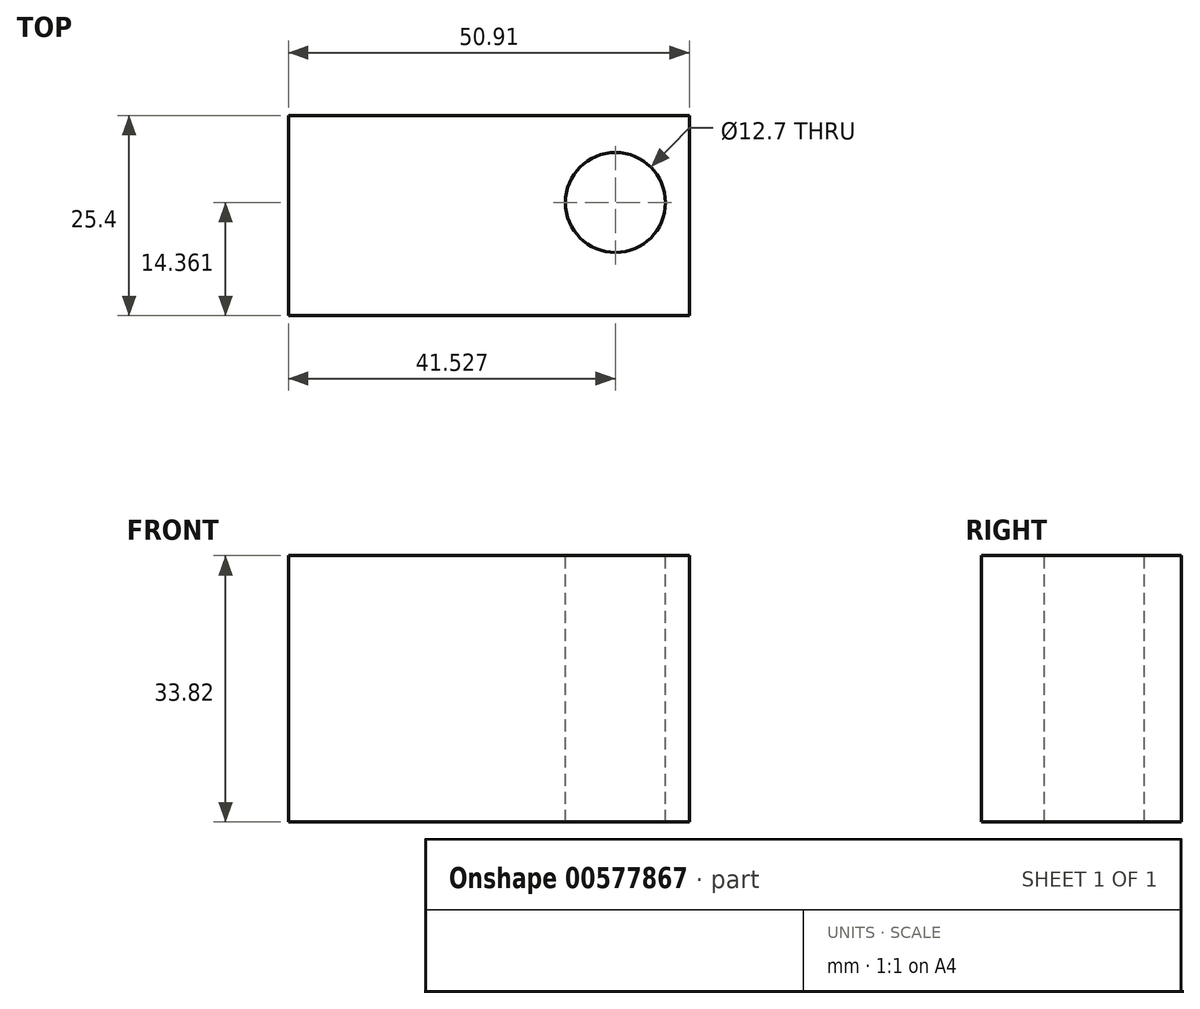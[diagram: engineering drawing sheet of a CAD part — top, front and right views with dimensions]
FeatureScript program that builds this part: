
annotation { "Feature Type Name" : "Feature", "Feature Type Description" : "" }
export const myFeature = defineFeature(function(context is Context, id is Id, definition is map)
    precondition{}
    {
        {
            var Q0;
            Q0=qCreatedBy(makeId("Front.planeOp"),FACE);
            var sketch = newSketch(context, id + "F0", { "sketchPlane" : qUnion([Q0])});
            skLineSegment(sketch, "E0.bottom", {"start": v(-50.91, 33.82) * mm, "end": v(0, 33.82) * mm});
            skLineSegment(sketch, "E0.top", {"start": v(-50.91, 0) * mm, "end": v(0, 0) * mm});
            skLineSegment(sketch, "E0.left", {"start": v(-50.91, 33.82) * mm, "end": v(-50.91, 0) * mm});
            skLineSegment(sketch, "E0.right", {"start": v(0, 33.82) * mm, "end": v(0, 0) * mm});
            skSolve(sketch);
        }
        {
            var Q0;
            Q0=makeQuery(id+"F0.imprint","IMPRINT",FACE,{"disambiguationData":[TD([[makeQuery(id+"F0.imprint","IMPRINT",EDGE,{"derivedFrom":sQuery(id+"F0.wireOp",EDGE,"E0.bottom")}),-1.0]])]});
            extrude(context, id + "F1", {"entities" : qUnion([Q0]), "depth" : 25.4 * mm, "offsetDistance" : 25.4 * mm});
        }
        {
            var Q0;
            Q0=makeQuery(id+"F1.opExtrude","SWEPT_FACE",FACE,{"disambiguationData":[OSD([sQuery(id+"F0.wireOp",EDGE,"E0.bottom")])]});
            var sketch = newSketch(context, id + "F2", { "sketchPlane" : qUnion([Q0])});
            skPoint(sketch, "E1", {"position": v(-25.46, 0) * mm});
            skPoint(sketch, "E2", {"position": v(-9.38, -11.04) * mm});
            skSolve(sketch);
        }
        {
            var Q0;
            Q0=sQuery(id+"F2.wireOp",VERTEX,"E2");
            var Q1;
            Q1=makeQuery(id+"F1.opExtrude","SWEPT_BODY",BODY,{"disambiguationData":[OSD([sQuery(id+"F0.wireOp",EDGE,"E0.bottom"),sQuery(id+"F0.wireOp",EDGE,"E0.top"),sQuery(id+"F0.wireOp",EDGE,"E0.left"),sQuery(id+"F0.wireOp",EDGE,"E0.right")])]});
            hole(context, id + "F3", {"style" : HoleStyle.SIMPLE, "endStyle" : HoleEndStyle.THROUGH, "holeDiameter" : 12.7 * mm, "isTappedThrough" : true, "tappedDepth" : 12.7 * mm, "tapClearance" : 3, "locations" : qUnion([Q0]), "scope" : qUnion([Q1])});
        }
    });
